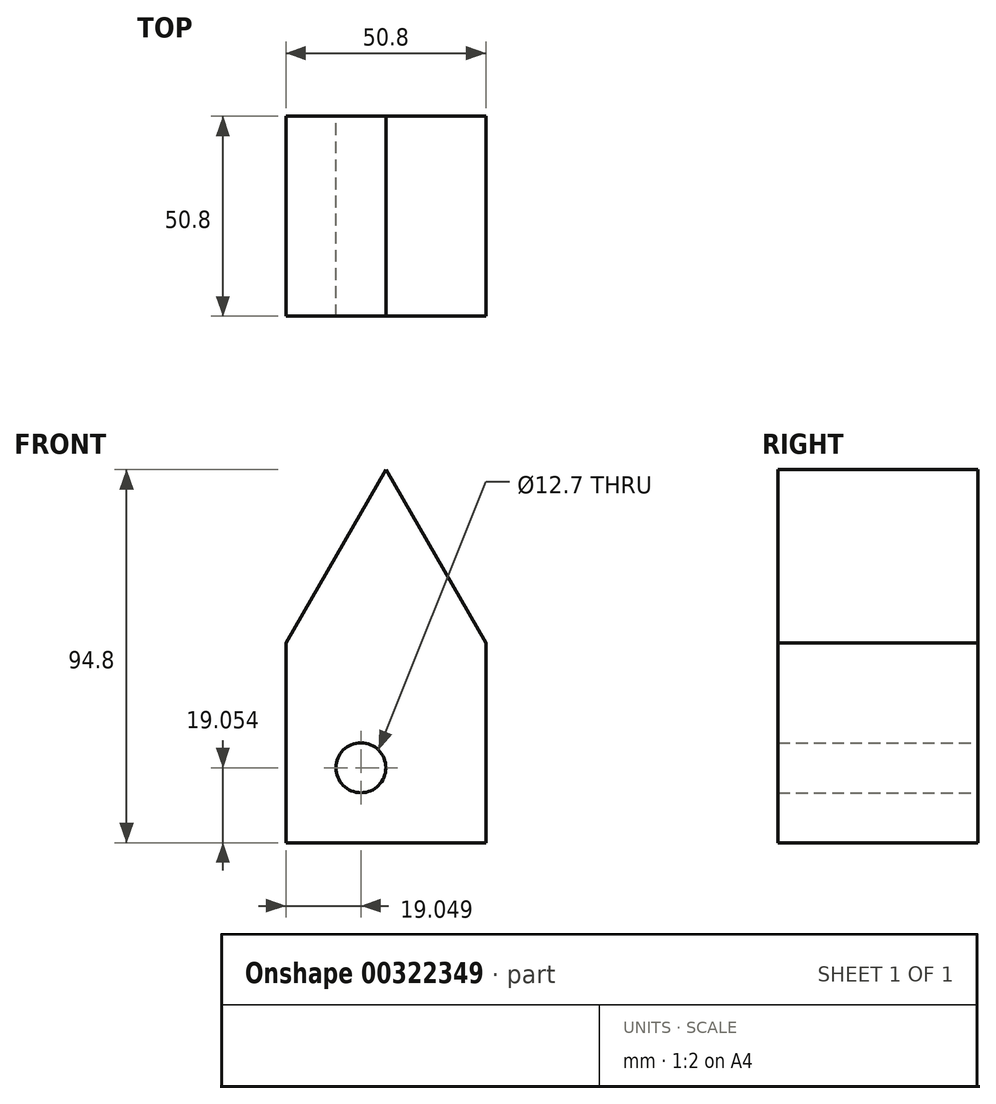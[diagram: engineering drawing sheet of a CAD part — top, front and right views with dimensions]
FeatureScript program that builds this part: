
annotation { "Feature Type Name" : "Feature", "Feature Type Description" : "" }
export const myFeature = defineFeature(function(context is Context, id is Id, definition is map)
    precondition{}
    {
        {
            var Q0;
            Q0=qCreatedBy(makeId("Front.planeOp"),FACE);
            var sketch = newSketch(context, id + "F0", { "sketchPlane" : qUnion([Q0])});
            skLineSegment(sketch, "E0.top", {"start": v(-20.71, -33.85) * mm, "end": v(30.09, -33.85) * mm});
            skLineSegment(sketch, "E0.left", {"start": v(-20.71, 16.95) * mm, "end": v(-20.71, -33.85) * mm});
            skLineSegment(sketch, "E0.right", {"start": v(30.09, 16.95) * mm, "end": v(30.09, -33.85) * mm});
            skLineSegment(sketch, "E1", {"start": v(-20.71, 16.95) * mm, "end": v(4.69, 60.95) * mm});
            skLineSegment(sketch, "E2", {"start": v(30.09, 16.95) * mm, "end": v(4.69, 60.95) * mm});
            skCircle(sketch, "E3", {"center": v(-1.66, -14.8) * mm, "radius": 6.35 * mm});
            skSolve(sketch);
        }
        {
            var Q0;
            Q0=makeQuery(id+"F0.imprint","IMPRINT",FACE,{"disambiguationData":[TD([[makeQuery(id+"F0.imprint","IMPRINT",EDGE,{"derivedFrom":sQuery(id+"F0.wireOp",EDGE,"E0.top")}),1.0]])]});
            extrude(context, id + "F1", {"entities" : qUnion([Q0]), "depth" : 50.8 * mm});
        }
    });
